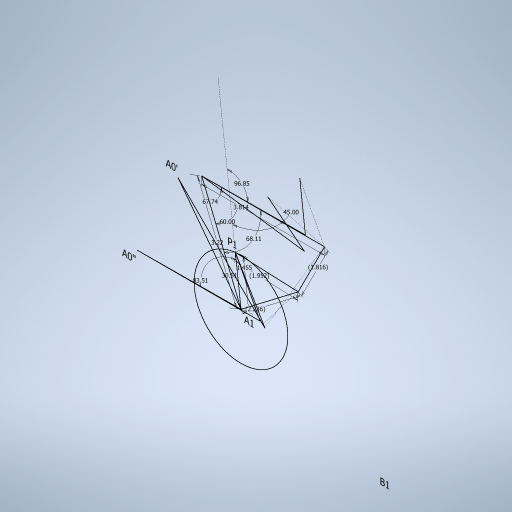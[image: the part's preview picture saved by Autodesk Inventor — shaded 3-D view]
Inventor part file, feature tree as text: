
AUTODESK INVENTOR PART (.ipt)
format: ipt  version: 2024 (Build 280153000, 153)  size: 262,144 bytes
history: native  units: in
note: dims shown in document units (in); Inventor stores cm internally (conversion verified against a paired STEP export)
features: sketch x1
ambient origin geometry x8: Origin, YZ Plane, XZ Plane, XY Plane, X Axis, Y Axis, Z Axis, Center Point
feature tree (1):
  sketch  "Sketch1"  dims[d0=0.1268in d1=0.0573in d2=0.1502in d7=0.4655in d10=0.6655in d11=60.0deg d13=135.0deg d14=0.468in d15=0.2096in d16=0.5738in d18=0.088in d19=0.0715in d20=0.0768in]
